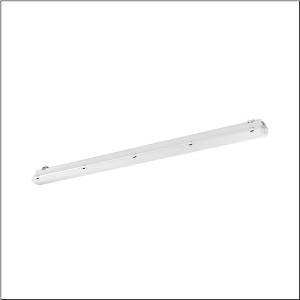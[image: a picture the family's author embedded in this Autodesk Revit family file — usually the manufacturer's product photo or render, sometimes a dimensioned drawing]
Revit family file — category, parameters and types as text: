
# Revit family: monsun_r__11xtreme_mo_51fe10dp440j_05e8
name_source: partatom
category: Lighting Fixtures
units: mm (PartAtom-declared; Revit-internal decimal feet)

## family parameters
Cut with Voids When Loaded = No
Host = Face
Light Source = No
Part Type = Normal
Room Calculation Point = No
Round Connector Dimension = Use Diameter
Shared = No

## types (1)
- --- (1 x LED, 4200 lm, 24.2 W, 4000K)
    Apparent Load = 24 VA
    CIE Flux Codes = 47 77 93 94 100
    Color Rendering = 80
    Color Temperature = 4000K
    Default Elevation = 1800 mm
    Description = Monsun® 11Xtreme MO, damp-proof luminaire, chain hanger, primary optical cover: enclosure, of PMMA, light emission: direct distribution, primary light characteristic: symmetric, installation type: suspended mounting, surface-mounted, horizontal mounting, vertical mounting, LED, rated luminous flux: 4.200lm, luminous efficacy: 174lm/W, light colour: 840, colour temperature: 4000K, control gear: ECG DALI, with terminal, 5-pole, max. 2.5mm², mains connection: 220..240V, AC, 50/60Hz, rated input power: 24W, luminaire housing, of glass-fibre reinforced polyester, uncoated, bright grey, incl. chain hanger, length: 1.590mm, width: 90mm, height: 88mm, clip for enclosure, of stainless steel (V2A), ceiling mounting element, of stainless steel (V2A), chain hanger, of stainless steel (V2A), protection rating (complete): IP66, insulation class (complete): insulation class I (protective earthing), certification: CE, ENEC, VDE, UKCA, protection symbol: D, impact resistance: IK04, permissible operating ambient temperature: -25..+50°C, standard: EN 60598-2-1, EN 50419, corresponds to IFS (International Featured Standards) requirements for safety and quality in the food industry, for indoor or canopied outdoor use, no direct snow, no direct sun, no direct rain, contact your sales advisor before using the luminaires in applications with unclear chemical exposure, large temperature fluctuations or condensation-forming humidity, LABS conformity tested according to VDMA 24364:2018-05, packaging unit: 1 piece
    Height = 88 mm
    Lamp = 1 x LED
    Lamp Light Flux = 4200 lm
    Lamp Power = 24.2 W
    Lamp count = 1
    Length = 1590 mm
    Luminous efficacy = 174 lm/W
    Manufacturer = Siteco
    ModVariant = No
    Model = 51FE10DP440J
    Mounting Place = Ceiling
    Mounting Type = Surface mounted
    Number of Poles = 1
    OnlyDefault = Yes
    Power Factor = 1
    Product Name = Monsun® 11Xtreme MO
    Product group = damp-proof luminaire
    ProductGroupID = 300
    Protection Class = Protection class I
    Protection Degree = IP 66
    RLX_Detail_Level = 1
    RLX_Emergency_Light_Flux = 0 lm
    RLX_Emergency_Type = 0
    RLX_Emergency_Type_DB = No
    RlxData = <blob elided: 87357 chars, md5=ea447b37>
    Socket = socket
    Standby Power = 0 W
    System Light Flux = 4200 lm
    System Power = 24 W
    Type Comments = factory setting: luminous flux: 100 % | dim-lin: 254 | 159 mA
    Type Image = l_1319630.jpg
    URL = http://relux.com
    VarID = @adj_170299
    Voltage = 0 V
    Weight = 0.00 kg
    Width = 90 mm

## geometry (parser evidence)
native form markers: Blend x4, Sweep x16
no freeform markers — native parametric forms only
